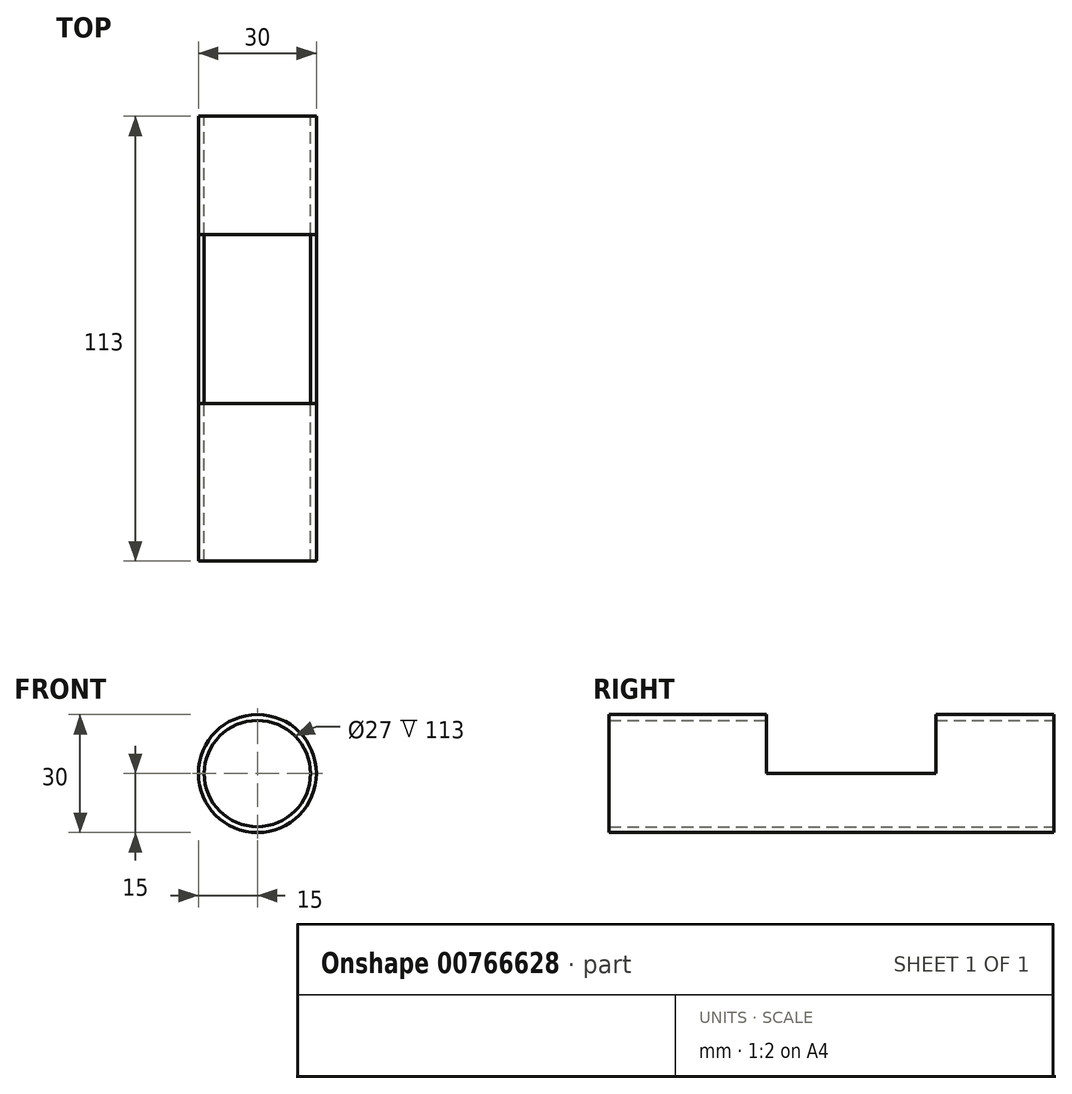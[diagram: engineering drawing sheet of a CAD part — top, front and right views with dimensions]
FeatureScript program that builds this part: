
annotation { "Feature Type Name" : "Feature", "Feature Type Description" : "" }
export const myFeature = defineFeature(function(context is Context, id is Id, definition is map)
    precondition{}
    {
        {
            var Q0;
            Q0=qCreatedBy(makeId("Front.planeOp"),FACE);
            var sketch = newSketch(context, id + "F0", { "sketchPlane" : qUnion([Q0])});
            skCircle(sketch, "E0", {"center": v(0, 0) * mm, "radius": 15 * mm});
            skCircle(sketch, "E1", {"center": v(0, 0) * mm, "radius": 13.5 * mm});
            skLineSegment(sketch, "E2", {"start": v(-15, 0) * mm, "end": v(-13.5, 0) * mm});
            skLineSegment(sketch, "E3", {"start": v(13.5, 0) * mm, "end": v(15, 0) * mm});
            skSolve(sketch);
        }
        {
            var Q0;
            {var subQ0=sQuery(id+"F0.wireOp",EDGE,"E2");Q0=makeQuery(id+"F0.imprint","IMPRINT",FACE,{"disambiguationData":[TD([[makeQuery(id+"F0.imprint","IMPRINT",EDGE,{"derivedFrom":subQ0}),-1.0]])]});}
            var Q1;
            {var subQ0=sQuery(id+"F0.wireOp",EDGE,"E2");Q1=makeQuery(id+"F0.imprint","IMPRINT",FACE,{"disambiguationData":[TD([[makeQuery(id+"F0.imprint","IMPRINT",EDGE,{"derivedFrom":subQ0}),1.0]])]});}
            extrude(context, id + "F1", {"entities" : qUnion([Q0, Q1]), "depth" : 40 * mm, "offsetDistance" : 25 * mm});
        }
        {
            var Q0;
            {var subQ0=sQuery(id+"F0.wireOp",EDGE,"E2");Q0=makeQuery(id+"F0.imprint","IMPRINT",FACE,{"disambiguationData":[TD([[makeQuery(id+"F0.imprint","IMPRINT",EDGE,{"derivedFrom":subQ0}),-1.0]])]});}
            extrude(context, id + "F2", {"entities" : qUnion([Q0]), "operationType" : NewBodyOperationType.ADD, "depth" : -43 * mm, "offsetDistance" : 25 * mm});
        }
        {
            var Q0;
            Q0=makeQuery(id+"F2.opExtrude","CAP_FACE",FACE,{"disambiguationData":[OSD([sQuery(id+"F0.wireOp",EDGE,"E0"),sQuery(id+"F0.wireOp",EDGE,"E1"),sQuery(id+"F0.wireOp",EDGE,"E2"),sQuery(id+"F0.wireOp",EDGE,"E3")])],"isStart":false});
            var sketch = newSketch(context, id + "F3", { "sketchPlane" : qUnion([Q0])});
            skCircle(sketch, "E4", {"center": v(0, 0) * mm, "radius": 15 * mm});
            skCircle(sketch, "E5", {"center": v(0, 0) * mm, "radius": 13.5 * mm});
            skSolve(sketch);
        }
        {
            var Q0;
            Q0 = qSketchRegion(id + "F3", true);
            extrude(context, id + "F4", {"entities" : qUnion([Q0]), "operationType" : NewBodyOperationType.ADD, "depth" : 30 * mm, "offsetDistance" : 25 * mm});
        }
    });
